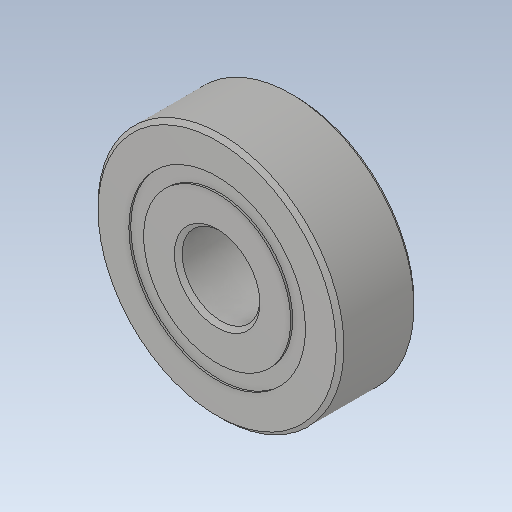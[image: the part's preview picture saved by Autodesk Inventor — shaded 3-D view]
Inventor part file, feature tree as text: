
AUTODESK INVENTOR PART (.ipt)
format: ipt  version: 2020.2 (Build 242310000, 310)  size: 726,016 bytes
history: imported  units: mm
features: imported_body x1
ambient origin geometry x8: Origin, YZ Plane, XZ Plane, XY Plane, X Axis, Y Axis, Z Axis, Center Point
bodies: Solide1 (imported_parasolid), Solide2 (imported_parasolid), Solide3 (imported_parasolid), Solide4 (imported_parasolid), Solide5 (imported_parasolid), Solide6 (imported_parasolid), Solide7 (imported_parasolid), Solide8 (imported_parasolid), Solide9 (imported_parasolid), Solide10 (imported_parasolid), Solide11 (imported_parasolid), Solide12 (imported_parasolid), Solide13 (imported_parasolid), Solide14 (imported_parasolid), Solide15 (imported_parasolid), Solide16 (imported_parasolid), Solide17 (imported_parasolid), Solide18 (imported_parasolid), Body1 (imported_parasolid), Body2 (imported_parasolid), Body3 (imported_parasolid), Body4 (imported_parasolid), Body5 (imported_parasolid), Body6 (imported_parasolid), Body7 (imported_parasolid), Body8 (imported_parasolid), Body9 (imported_parasolid), Body10 (imported_parasolid), Body11 (imported_parasolid), Body12 (imported_parasolid), Body13 (imported_parasolid), Body14 (imported_parasolid), Body15 (imported_parasolid), Body16 (imported_parasolid), Body17 (imported_parasolid), Body18 (imported_parasolid)
feature tree (1):
  imported_body  NMx_Import_Brep_tag  [imported B-rep: ~38 faces, bbox_mm=[18.7, 0.0, 6.0]]
